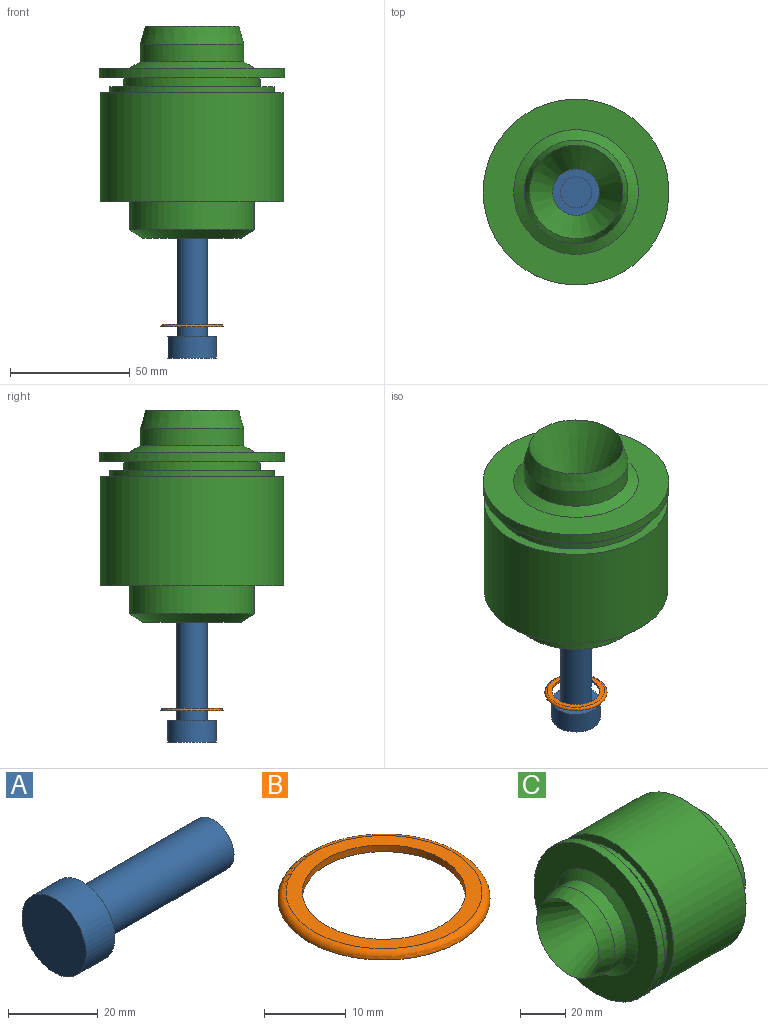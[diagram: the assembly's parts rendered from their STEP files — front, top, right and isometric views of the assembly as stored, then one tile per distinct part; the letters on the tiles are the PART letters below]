
ASSEMBLY  parts=3 mates=3
PART A: 5 faces, bbox 50.2x20.2x20.2 mm
  f0: plane 20.22x20.22mm, normal (-1,0,0), area 321.2mm2, adj f4
  f1: plane 12.91x12.91mm, normal (1,0,0), area 131mm2, adj f2
  f2: cylinder r=6.46mm len=41.16mm, axis (1,0,0), area 1669.8mm2, adj f1,f3
  f3: plane 20.22x20.22mm, normal (1,0,0), area 190.2mm2, adj f2,f4
  f4: cylinder r=10.11mm len=20.22mm, axis (1,0,0), area 572.6mm2, adj f0,f3
PART B: 4 faces, bbox 28.1x28.1x1.7 mm
  f0: plane 26x26mm, normal (0,0,-1), area 216.8mm2, adj f1,f3
  f1: cylinder r=10mm len=20mm, axis (0,0,1), area 62.8mm2, adj f0,f2
  f2: plane 24x24mm, normal (0,0,1), area 138.2mm2, adj f1,f3
  f3: torus R=12mm, axis (0,0,-1), area 124.7mm2, adj f0,f2
PART C: 20 faces, bbox 88.7x77.6x77.6 mm
  f0: cylinder r=21.67mm len=43.34mm, axis (1,0,0), area 989.2mm2, adj f1,f19
  f1: cone r=21.67mm half-angle=15.3deg, axis (1,0,0), area 1032.2mm2, adj f0,f2
  f2: cone r=19.57mm half-angle=23.7deg, axis (-1,0,0), area 2246.1mm2, adj f1,f3
  f3: cylinder r=9.76mm len=66.36mm, axis (1,0,0), area 4069.5mm2, adj f2,f4
  f4: cone r=12.7mm half-angle=23.3deg, axis (-1,0,0), area 524.8mm2, adj f3,f5
  f5: cone r=15.4mm half-angle=28.5deg, axis (-1,0,0), area 498mm2, adj f4,f6
  f6: cone r=20.6mm half-angle=44deg, axis (1,0,0), area 846.5mm2, adj f5,f7
  f7: cylinder r=20.6mm len=41.2mm, axis (1,0,0), area 828.8mm2, adj f6,f8
  f8: cone r=26.08mm half-angle=57.8deg, axis (-1,0,0), area 949.7mm2, adj f7,f9
  f9: cylinder r=26.08mm len=52.15mm, axis (1,0,0), area 1932mm2, adj f8,f10
  f10: plane 76.69x76.69mm, normal (1,0,0), area 2482.8mm2, adj f9,f11
  f11: cylinder r=38.34mm len=76.69mm, axis (1,0,0), area 10968.5mm2, adj f10,f12
  f12: plane 76.69x76.69mm, normal (-1,0,0), area 898.4mm2, adj f11,f13
  f13: cylinder r=34.41mm len=68.83mm, axis (1,0,0), area 560.3mm2, adj f12,f14
  f14: plane 68.83x68.83mm, normal (-1,0,0), area 1154.9mm2, adj f13,f15
  f15: cylinder r=28.58mm len=57.16mm, axis (1,0,0), area 641.6mm2, adj f14,f16
  f16: plane 77.64x77.64mm, normal (1,0,0), area 2168.8mm2, adj f15,f17
  f17: cylinder r=38.82mm len=77.64mm, axis (1,0,0), area 1016.8mm2, adj f16,f18
  f18: plane 77.64x77.64mm, normal (-1,0,0), area 2598.3mm2, adj f17,f19
  f19: cone r=21.67mm half-angle=59.3deg, axis (1,0,0), area 769.1mm2, adj f0,f18
PLACE A rot(axis=(0,-1,0),90deg) t=(-21.21,28.28,-63.56)mm
PLACE B t=(-21.21,28.28,-100.72)mm
PLACE C rot(axis=(0,1,0),90deg) t=(-21.21,28.28,-2.81)mm
MATE slider C.f0 <-> A.f2  axis (0,0,-1) through (-21.21,28.28,-63.58)mm
MATE fastened B.f1 <-> A.f2  axis (0,0,-1) through (-21.21,28.28,-100.72)mm
MATE slider C.f0 <-> B.f1  axis (0,0,-1) through (-21.21,28.28,-63.58)mm
